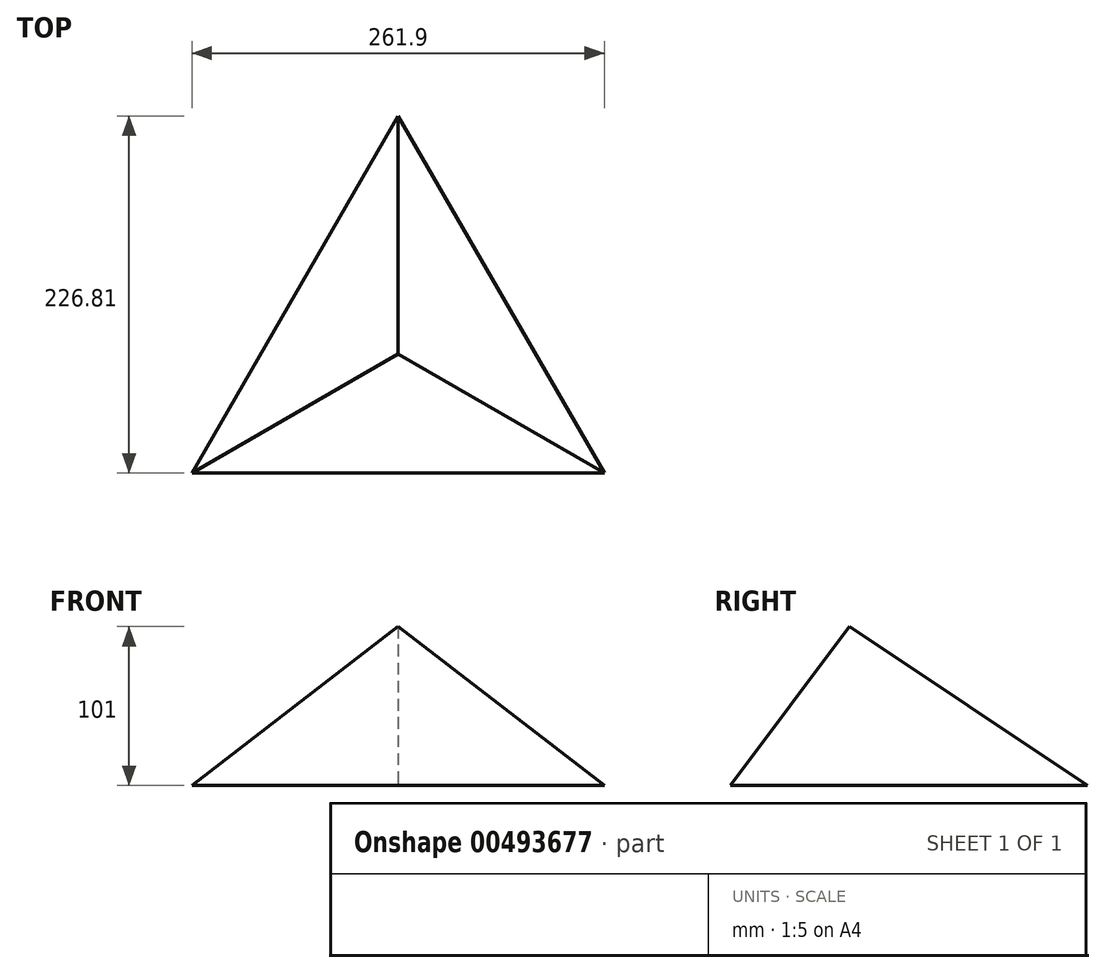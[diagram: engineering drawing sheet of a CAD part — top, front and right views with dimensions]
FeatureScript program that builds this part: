
annotation { "Feature Type Name" : "Feature", "Feature Type Description" : "" }
export const myFeature = defineFeature(function(context is Context, id is Id, definition is map)
    precondition{}
    {
        {
            var Q0;
            Q0=qCreatedBy(makeId("Top.planeOp"),FACE);
            var sketch = newSketch(context, id + "F0", { "sketchPlane" : qUnion([Q0])});
            skCircle(sketch, "E0.cCircle", {"center": v(0, 0) * mm, "radius": 151.2 * mm, "construction": true});
            skLineSegment(sketch, "E0.0", {"start": v(0, 151.2) * mm, "end": v(130.95, -75.6) * mm});
            skLineSegment(sketch, "E0.1", {"start": v(130.95, -75.6) * mm, "end": v(-130.95, -75.6) * mm});
            skLineSegment(sketch, "E0.2", {"start": v(-130.95, -75.6) * mm, "end": v(0, 151.2) * mm});
            skSolve(sketch);
        }
        {
            var Q0;
            Q0=qCreatedBy(makeId("Top.planeOp"),FACE);
            cPlane(context, id + "F1", {"entities" : qUnion([Q0]), "cplaneType" : CPlaneType.OFFSET, "offset" : 101 * mm, "width" : 150 * mm, "height" : 150 * mm});
        }
        {
            var Q0;
            Q0=qCreatedBy(id+"F1.planeOp",FACE);
            var sketch = newSketch(context, id + "F2", { "sketchPlane" : qUnion([Q0])});
            skPoint(sketch, "E1", {"position": v(0, 0) * mm});
            skSolve(sketch);
        }
        {
            var Q0;
            Q0=sQuery(id+"F2.wireOp",VERTEX,"E1");
            var Q1;
            Q1=makeQuery(id+"F0.imprint","IMPRINT",FACE,{"disambiguationData":[TD([[makeQuery(id+"F0.imprint","IMPRINT",EDGE,{"derivedFrom":sQuery(id+"F0.wireOp",EDGE,"E0.0")}),-1.0]])]});
            loft(context, id + "F3", {"sheetProfilesArray" : [{ "sheetProfileEntities" : qUnion([Q0]) }, { "sheetProfileEntities" : qUnion([Q1]) }]});
        }
    });
